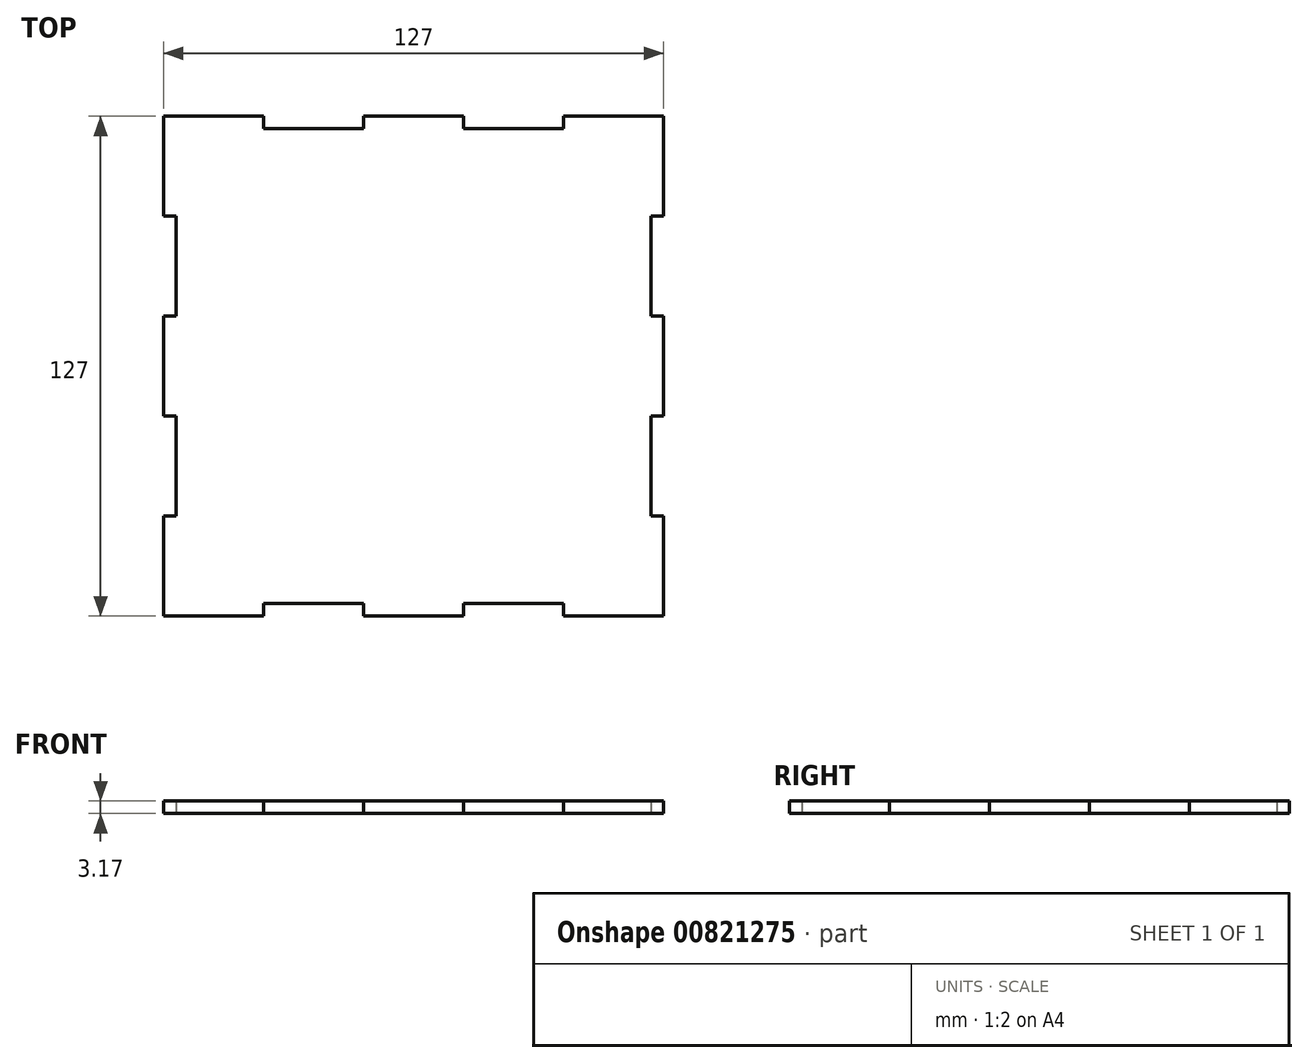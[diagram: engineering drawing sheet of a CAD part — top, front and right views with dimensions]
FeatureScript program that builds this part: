
annotation { "Feature Type Name" : "Feature", "Feature Type Description" : "" }
export const myFeature = defineFeature(function(context is Context, id is Id, definition is map)
    precondition{}
    {
        {
            var Q0;
            Q0=qCreatedBy(makeId("Top.planeOp"),FACE);
            var sketch = newSketch(context, id + "F0", { "sketchPlane" : qUnion([Q0])});
            skLineSegment(sketch, "E0.bottom", {"start": v(-63.5, 63.5) * mm, "end": v(63.5, 63.5) * mm});
            skLineSegment(sketch, "E0.top", {"start": v(-63.5, -63.5) * mm, "end": v(63.5, -63.5) * mm});
            skLineSegment(sketch, "E0.left", {"start": v(-63.5, 63.5) * mm, "end": v(-63.5, -63.5) * mm});
            skLineSegment(sketch, "E0.right", {"start": v(63.5, 63.5) * mm, "end": v(63.5, -63.5) * mm});
            skPoint(sketch, "E0.middle", {"position": v(0, 0) * mm});
            skLineSegment(sketch, "E1", {"start": v(-38.1, 63.5) * mm, "end": v(-38.1, -63.5) * mm});
            skLineSegment(sketch, "E2", {"start": v(-63.5, -38.1) * mm, "end": v(63.5, -38.1) * mm});
            skLineSegment(sketch, "E3.1.0.0", {"start": v(-12.7, 63.5) * mm, "end": v(-12.7, -63.5) * mm});
            skLineSegment(sketch, "E3.2.0.0", {"start": v(12.7, 63.5) * mm, "end": v(12.7, -63.5) * mm});
            skLineSegment(sketch, "E3.3.0.0", {"start": v(38.1, 63.5) * mm, "end": v(38.1, -63.5) * mm});
            skLineSegment(sketch, "E3.direction1", {"start": v(-38.1, -63.5) * mm, "end": v(-12.7, -63.5) * mm, "construction": true});
            skLineSegment(sketch, "E4.0.1.0", {"start": v(-63.5, -12.7) * mm, "end": v(63.5, -12.7) * mm});
            skLineSegment(sketch, "E4.0.2.0", {"start": v(-63.5, 12.7) * mm, "end": v(63.5, 12.7) * mm});
            skLineSegment(sketch, "E4.0.3.0", {"start": v(-63.5, 38.1) * mm, "end": v(63.5, 38.1) * mm});
            skLineSegment(sketch, "E4.1.0.0", {"start": v(-38.1, -38.1) * mm, "end": v(63.5, -38.1) * mm});
            skLineSegment(sketch, "E4.1.1.0", {"start": v(-38.1, -12.7) * mm, "end": v(63.5, -12.7) * mm});
            skLineSegment(sketch, "E4.1.2.0", {"start": v(-38.1, 12.7) * mm, "end": v(63.5, 12.7) * mm});
            skLineSegment(sketch, "E4.1.3.0", {"start": v(-38.1, 38.1) * mm, "end": v(63.5, 38.1) * mm});
            skLineSegment(sketch, "E4.2.0.0", {"start": v(-12.7, -38.1) * mm, "end": v(63.5, -38.1) * mm});
            skLineSegment(sketch, "E4.2.1.0", {"start": v(-12.7, -12.7) * mm, "end": v(63.5, -12.7) * mm});
            skLineSegment(sketch, "E4.2.2.0", {"start": v(-12.7, 12.7) * mm, "end": v(63.5, 12.7) * mm});
            skLineSegment(sketch, "E4.2.3.0", {"start": v(-12.7, 38.1) * mm, "end": v(63.5, 38.1) * mm});
            skLineSegment(sketch, "E4.direction1", {"start": v(-63.5, -38.1) * mm, "end": v(-38.1, -38.1) * mm, "construction": true});
            skLineSegment(sketch, "E4.direction2", {"start": v(-63.5, -38.1) * mm, "end": v(-63.5, -12.7) * mm, "construction": true});
            skLineSegment(sketch, "E5", {"start": v(-63.5, -60.33) * mm, "end": v(63.5, -60.32) * mm});
            skLineSegment(sketch, "E6", {"start": v(-60.33, 63.5) * mm, "end": v(-60.33, -63.5) * mm});
            skLineSegment(sketch, "E7", {"start": v(-63.5, 60.33) * mm, "end": v(63.5, 60.33) * mm});
            skLineSegment(sketch, "E8", {"start": v(60.32, 63.5) * mm, "end": v(60.32, -63.5) * mm});
            skSolve(sketch);
        }
        {
            var Q0;
            {var subQ0=sQuery(id+"F0.wireOp",EDGE,"E6");var subQ1=sQuery(id+"F0.wireOp",EDGE,"E0.bottom");var subQ2=makeQuery(id+"F0.imprint","INTERSECT",VERTEX,{"derivedFrom":[subQ1,subQ0]});Q0=makeQuery(id+"F0.imprint","IMPRINT",FACE,{"disambiguationData":[TD([[makeQuery(id+"F0.imprint","IMPRINT",EDGE,{"disambiguationData":[TD([[subQ2,1.0]])],"derivedFrom":subQ1}),-1.0]])]});}
            var Q1;
            {var subQ0=sQuery(id+"F0.wireOp",EDGE,"E0.right");var subQ1=sQuery(id+"F0.wireOp",EDGE,"E0.bottom");var subQ2=makeQuery(id+"F0.imprint","INTERSECT",VERTEX,{"derivedFrom":[subQ1,subQ0]});Q1=makeQuery(id+"F0.imprint","IMPRINT",FACE,{"disambiguationData":[TD([[makeQuery(id+"F0.imprint","IMPRINT",EDGE,{"disambiguationData":[TD([[subQ2,1.0]])],"derivedFrom":subQ1}),-1.0]])]});}
            var Q2;
            {var subQ0=sQuery(id+"F0.wireOp",EDGE,"E6");var subQ1=sQuery(id+"F0.wireOp",EDGE,"E0.top");var subQ2=makeQuery(id+"F0.imprint","INTERSECT",VERTEX,{"derivedFrom":[subQ1,subQ0]});Q2=makeQuery(id+"F0.imprint","IMPRINT",FACE,{"disambiguationData":[TD([[makeQuery(id+"F0.imprint","IMPRINT",EDGE,{"disambiguationData":[TD([[subQ2,1.0]])],"derivedFrom":subQ1}),1.0]])]});}
            var Q3;
            {var subQ0=sQuery(id+"F0.wireOp",EDGE,"E0.right");var subQ1=sQuery(id+"F0.wireOp",EDGE,"E0.top");var subQ2=makeQuery(id+"F0.imprint","INTERSECT",VERTEX,{"derivedFrom":[subQ1,subQ0]});Q3=makeQuery(id+"F0.imprint","IMPRINT",FACE,{"disambiguationData":[TD([[makeQuery(id+"F0.imprint","IMPRINT",EDGE,{"disambiguationData":[TD([[subQ2,1.0]])],"derivedFrom":subQ1}),1.0]])]});}
            var Q4;
            {var subQ0=sQuery(id+"F0.wireOp",EDGE,"E1");var subQ1=sQuery(id+"F0.wireOp",EDGE,"E0.bottom");var subQ2=makeQuery(id+"F0.imprint","INTERSECT",VERTEX,{"derivedFrom":[subQ1,subQ0]});Q4=makeQuery(id+"F0.imprint","IMPRINT",FACE,{"disambiguationData":[TD([[makeQuery(id+"F0.imprint","IMPRINT",EDGE,{"disambiguationData":[TD([[subQ2,1.0]])],"derivedFrom":subQ1}),-1.0]])]});}
            var Q5;
            {var subQ0=sQuery(id+"F0.wireOp",EDGE,"E3.1.0.0");var subQ1=sQuery(id+"F0.wireOp",EDGE,"E0.bottom");var subQ2=makeQuery(id+"F0.imprint","INTERSECT",VERTEX,{"derivedFrom":[subQ1,subQ0]});Q5=makeQuery(id+"F0.imprint","IMPRINT",FACE,{"disambiguationData":[TD([[makeQuery(id+"F0.imprint","IMPRINT",EDGE,{"disambiguationData":[TD([[subQ2,-1.0]])],"derivedFrom":subQ1}),-1.0]])]});}
            var Q6;
            {var subQ0=sQuery(id+"F0.wireOp",EDGE,"E3.3.0.0");var subQ1=sQuery(id+"F0.wireOp",EDGE,"E0.bottom");var subQ2=makeQuery(id+"F0.imprint","INTERSECT",VERTEX,{"derivedFrom":[subQ1,subQ0]});Q6=makeQuery(id+"F0.imprint","IMPRINT",FACE,{"disambiguationData":[TD([[makeQuery(id+"F0.imprint","IMPRINT",EDGE,{"disambiguationData":[TD([[subQ2,-1.0]])],"derivedFrom":subQ1}),-1.0]])]});}
            var Q7;
            {var subQ0=sQuery(id+"F0.wireOp",EDGE,"E1");var subQ1=sQuery(id+"F0.wireOp",EDGE,"E0.top");var subQ2=makeQuery(id+"F0.imprint","INTERSECT",VERTEX,{"derivedFrom":[subQ1,subQ0]});Q7=makeQuery(id+"F0.imprint","IMPRINT",FACE,{"disambiguationData":[TD([[makeQuery(id+"F0.imprint","IMPRINT",EDGE,{"disambiguationData":[TD([[subQ2,1.0]])],"derivedFrom":subQ1}),1.0]])]});}
            var Q8;
            {var subQ0=sQuery(id+"F0.wireOp",EDGE,"E3.1.0.0");var subQ1=sQuery(id+"F0.wireOp",EDGE,"E0.top");var subQ2=makeQuery(id+"F0.imprint","INTERSECT",VERTEX,{"derivedFrom":[subQ1,subQ0]});Q8=makeQuery(id+"F0.imprint","IMPRINT",FACE,{"disambiguationData":[TD([[makeQuery(id+"F0.imprint","IMPRINT",EDGE,{"disambiguationData":[TD([[subQ2,-1.0]])],"derivedFrom":subQ1}),1.0]])]});}
            var Q9;
            {var subQ0=sQuery(id+"F0.wireOp",EDGE,"E3.3.0.0");var subQ1=sQuery(id+"F0.wireOp",EDGE,"E0.top");var subQ2=makeQuery(id+"F0.imprint","INTERSECT",VERTEX,{"derivedFrom":[subQ1,subQ0]});Q9=makeQuery(id+"F0.imprint","IMPRINT",FACE,{"disambiguationData":[TD([[makeQuery(id+"F0.imprint","IMPRINT",EDGE,{"disambiguationData":[TD([[subQ2,-1.0]])],"derivedFrom":subQ1}),1.0]])]});}
            var Q10;
            {var subQ0=sQuery(id+"F0.wireOp",EDGE,"E7");var subQ1=sQuery(id+"F0.wireOp",EDGE,"E0.left");var subQ2=makeQuery(id+"F0.imprint","INTERSECT",VERTEX,{"derivedFrom":[subQ1,subQ0]});Q10=makeQuery(id+"F0.imprint","IMPRINT",FACE,{"disambiguationData":[TD([[makeQuery(id+"F0.imprint","IMPRINT",EDGE,{"disambiguationData":[TD([[subQ2,-1.0]])],"derivedFrom":subQ1}),1.0]])]});}
            var Q11;
            {var subQ0=sQuery(id+"F0.wireOp",EDGE,"E4.0.2.0");var subQ1=sQuery(id+"F0.wireOp",EDGE,"E0.left");var subQ2=makeQuery(id+"F0.imprint","INTERSECT",VERTEX,{"derivedFrom":[subQ1,subQ0]});Q11=makeQuery(id+"F0.imprint","IMPRINT",FACE,{"disambiguationData":[TD([[makeQuery(id+"F0.imprint","IMPRINT",EDGE,{"disambiguationData":[TD([[subQ2,-1.0]])],"derivedFrom":subQ1}),1.0]])]});}
            var Q12;
            {var subQ0=sQuery(id+"F0.wireOp",EDGE,"E2");var subQ1=sQuery(id+"F0.wireOp",EDGE,"E0.left");var subQ2=makeQuery(id+"F0.imprint","INTERSECT",VERTEX,{"derivedFrom":[subQ1,subQ0]});Q12=makeQuery(id+"F0.imprint","IMPRINT",FACE,{"disambiguationData":[TD([[makeQuery(id+"F0.imprint","IMPRINT",EDGE,{"disambiguationData":[TD([[subQ2,-1.0]])],"derivedFrom":subQ1}),1.0]])]});}
            var Q13;
            {var subQ0=sQuery(id+"F0.wireOp",EDGE,"E7");var subQ1=sQuery(id+"F0.wireOp",EDGE,"E0.right");var subQ2=makeQuery(id+"F0.imprint","INTERSECT",VERTEX,{"derivedFrom":[subQ1,subQ0]});Q13=makeQuery(id+"F0.imprint","IMPRINT",FACE,{"disambiguationData":[TD([[makeQuery(id+"F0.imprint","IMPRINT",EDGE,{"disambiguationData":[TD([[subQ2,-1.0]])],"derivedFrom":subQ1}),-1.0]])]});}
            var Q14;
            {var subQ0=sQuery(id+"F0.wireOp",EDGE,"E4.0.2.0");var subQ1=sQuery(id+"F0.wireOp",EDGE,"E0.right");var subQ2=makeQuery(id+"F0.imprint","INTERSECT",VERTEX,{"derivedFrom":[subQ1,subQ0]});Q14=makeQuery(id+"F0.imprint","IMPRINT",FACE,{"disambiguationData":[TD([[makeQuery(id+"F0.imprint","IMPRINT",EDGE,{"disambiguationData":[TD([[subQ2,-1.0]])],"derivedFrom":subQ1}),-1.0]])]});}
            var Q15;
            {var subQ0=sQuery(id+"F0.wireOp",EDGE,"E5");var subQ1=sQuery(id+"F0.wireOp",EDGE,"E0.right");var subQ2=makeQuery(id+"F0.imprint","INTERSECT",VERTEX,{"derivedFrom":[subQ1,subQ0]});Q15=makeQuery(id+"F0.imprint","IMPRINT",FACE,{"disambiguationData":[TD([[makeQuery(id+"F0.imprint","IMPRINT",EDGE,{"disambiguationData":[TD([[subQ2,1.0]])],"derivedFrom":subQ1}),-1.0]])]});}
            var Q16;
            {var subQ0=sQuery(id+"F0.wireOp",EDGE,"E7");var subQ1=sQuery(id+"F0.wireOp",EDGE,"E1");var subQ2=makeQuery(id+"F0.imprint","INTERSECT",VERTEX,{"derivedFrom":[subQ1,subQ0]});Q16=makeQuery(id+"F0.imprint","IMPRINT",FACE,{"disambiguationData":[TD([[makeQuery(id+"F0.imprint","IMPRINT",EDGE,{"disambiguationData":[TD([[subQ2,-1.0]])],"derivedFrom":subQ1}),-1.0]])]});}
            var Q17;
            {var subQ0=sQuery(id+"F0.wireOp",EDGE,"E7");var subQ1=sQuery(id+"F0.wireOp",EDGE,"E1");var subQ2=makeQuery(id+"F0.imprint","INTERSECT",VERTEX,{"derivedFrom":[subQ1,subQ0]});Q17=makeQuery(id+"F0.imprint","IMPRINT",FACE,{"disambiguationData":[TD([[makeQuery(id+"F0.imprint","IMPRINT",EDGE,{"disambiguationData":[TD([[subQ2,-1.0]])],"derivedFrom":subQ1}),1.0]])]});}
            var Q18;
            {var subQ0=sQuery(id+"F0.wireOp",EDGE,"E7");var subQ1=sQuery(id+"F0.wireOp",EDGE,"E3.2.0.0");var subQ2=makeQuery(id+"F0.imprint","INTERSECT",VERTEX,{"derivedFrom":[subQ1,subQ0]});Q18=makeQuery(id+"F0.imprint","IMPRINT",FACE,{"disambiguationData":[TD([[makeQuery(id+"F0.imprint","IMPRINT",EDGE,{"disambiguationData":[TD([[subQ2,-1.0]])],"derivedFrom":subQ1}),1.0]])]});}
            var Q19;
            {var subQ0=sQuery(id+"F0.wireOp",EDGE,"E7");var subQ1=sQuery(id+"F0.wireOp",EDGE,"E3.3.0.0");var subQ2=makeQuery(id+"F0.imprint","INTERSECT",VERTEX,{"derivedFrom":[subQ1,subQ0]});Q19=makeQuery(id+"F0.imprint","IMPRINT",FACE,{"disambiguationData":[TD([[makeQuery(id+"F0.imprint","IMPRINT",EDGE,{"disambiguationData":[TD([[subQ2,-1.0]])],"derivedFrom":subQ1}),1.0]])]});}
            var Q20;
            {var subQ0=sQuery(id+"F0.wireOp",EDGE,"E4.0.2.0");var subQ1=sQuery(id+"F0.wireOp",EDGE,"E3.3.0.0");var subQ2=makeQuery(id+"F0.imprint","INTERSECT",VERTEX,{"derivedFrom":[subQ1,subQ0]});Q20=makeQuery(id+"F0.imprint","IMPRINT",FACE,{"disambiguationData":[TD([[makeQuery(id+"F0.imprint","IMPRINT",EDGE,{"disambiguationData":[TD([[subQ2,1.0]])],"derivedFrom":subQ1}),1.0]])]});}
            var Q21;
            {var subQ0=sQuery(id+"F0.wireOp",EDGE,"E4.0.2.0");var subQ1=sQuery(id+"F0.wireOp",EDGE,"E3.2.0.0");var subQ2=makeQuery(id+"F0.imprint","INTERSECT",VERTEX,{"derivedFrom":[subQ1,subQ0]});Q21=makeQuery(id+"F0.imprint","IMPRINT",FACE,{"disambiguationData":[TD([[makeQuery(id+"F0.imprint","IMPRINT",EDGE,{"disambiguationData":[TD([[subQ2,1.0]])],"derivedFrom":subQ1}),1.0]])]});}
            var Q22;
            {var subQ0=sQuery(id+"F0.wireOp",EDGE,"E4.0.2.0");var subQ1=sQuery(id+"F0.wireOp",EDGE,"E3.1.0.0");var subQ2=makeQuery(id+"F0.imprint","INTERSECT",VERTEX,{"derivedFrom":[subQ1,subQ0]});Q22=makeQuery(id+"F0.imprint","IMPRINT",FACE,{"disambiguationData":[TD([[makeQuery(id+"F0.imprint","IMPRINT",EDGE,{"disambiguationData":[TD([[subQ2,1.0]])],"derivedFrom":subQ1}),1.0]])]});}
            var Q23;
            {var subQ0=sQuery(id+"F0.wireOp",EDGE,"E4.0.2.0");var subQ1=sQuery(id+"F0.wireOp",EDGE,"E1");var subQ2=makeQuery(id+"F0.imprint","INTERSECT",VERTEX,{"derivedFrom":[subQ1,subQ0]});Q23=makeQuery(id+"F0.imprint","IMPRINT",FACE,{"disambiguationData":[TD([[makeQuery(id+"F0.imprint","IMPRINT",EDGE,{"disambiguationData":[TD([[subQ2,1.0]])],"derivedFrom":subQ1}),1.0]])]});}
            var Q24;
            {var subQ0=sQuery(id+"F0.wireOp",EDGE,"E4.0.2.0");var subQ1=sQuery(id+"F0.wireOp",EDGE,"E1");var subQ2=makeQuery(id+"F0.imprint","INTERSECT",VERTEX,{"derivedFrom":[subQ1,subQ0]});Q24=makeQuery(id+"F0.imprint","IMPRINT",FACE,{"disambiguationData":[TD([[makeQuery(id+"F0.imprint","IMPRINT",EDGE,{"disambiguationData":[TD([[subQ2,1.0]])],"derivedFrom":subQ1}),-1.0]])]});}
            var Q25;
            {var subQ0=sQuery(id+"F0.wireOp",EDGE,"E4.0.2.0");var subQ1=sQuery(id+"F0.wireOp",EDGE,"E1");var subQ2=makeQuery(id+"F0.imprint","INTERSECT",VERTEX,{"derivedFrom":[subQ1,subQ0]});Q25=makeQuery(id+"F0.imprint","IMPRINT",FACE,{"disambiguationData":[TD([[makeQuery(id+"F0.imprint","IMPRINT",EDGE,{"disambiguationData":[TD([[subQ2,-1.0]])],"derivedFrom":subQ1}),-1.0]])]});}
            var Q26;
            {var subQ0=sQuery(id+"F0.wireOp",EDGE,"E4.0.2.0");var subQ1=sQuery(id+"F0.wireOp",EDGE,"E1");var subQ2=makeQuery(id+"F0.imprint","INTERSECT",VERTEX,{"derivedFrom":[subQ1,subQ0]});Q26=makeQuery(id+"F0.imprint","IMPRINT",FACE,{"disambiguationData":[TD([[makeQuery(id+"F0.imprint","IMPRINT",EDGE,{"disambiguationData":[TD([[subQ2,-1.0]])],"derivedFrom":subQ1}),1.0]])]});}
            var Q27;
            {var subQ0=sQuery(id+"F0.wireOp",EDGE,"E4.0.1.0");var subQ1=sQuery(id+"F0.wireOp",EDGE,"E3.1.0.0");var subQ2=makeQuery(id+"F0.imprint","INTERSECT",VERTEX,{"derivedFrom":[subQ1,subQ0]});Q27=makeQuery(id+"F0.imprint","IMPRINT",FACE,{"disambiguationData":[TD([[makeQuery(id+"F0.imprint","IMPRINT",EDGE,{"disambiguationData":[TD([[subQ2,1.0]])],"derivedFrom":subQ1}),1.0]])]});}
            var Q28;
            {var subQ0=sQuery(id+"F0.wireOp",EDGE,"E4.0.1.0");var subQ1=sQuery(id+"F0.wireOp",EDGE,"E3.2.0.0");var subQ2=makeQuery(id+"F0.imprint","INTERSECT",VERTEX,{"derivedFrom":[subQ1,subQ0]});Q28=makeQuery(id+"F0.imprint","IMPRINT",FACE,{"disambiguationData":[TD([[makeQuery(id+"F0.imprint","IMPRINT",EDGE,{"disambiguationData":[TD([[subQ2,1.0]])],"derivedFrom":subQ1}),1.0]])]});}
            var Q29;
            {var subQ0=sQuery(id+"F0.wireOp",EDGE,"E4.0.1.0");var subQ1=sQuery(id+"F0.wireOp",EDGE,"E3.3.0.0");var subQ2=makeQuery(id+"F0.imprint","INTERSECT",VERTEX,{"derivedFrom":[subQ1,subQ0]});Q29=makeQuery(id+"F0.imprint","IMPRINT",FACE,{"disambiguationData":[TD([[makeQuery(id+"F0.imprint","IMPRINT",EDGE,{"disambiguationData":[TD([[subQ2,1.0]])],"derivedFrom":subQ1}),1.0]])]});}
            var Q30;
            {var subQ0=sQuery(id+"F0.wireOp",EDGE,"E3.3.0.0");var subQ1=sQuery(id+"F0.wireOp",EDGE,"E2");var subQ2=makeQuery(id+"F0.imprint","INTERSECT",VERTEX,{"derivedFrom":[subQ1,subQ0]});Q30=makeQuery(id+"F0.imprint","IMPRINT",FACE,{"disambiguationData":[TD([[makeQuery(id+"F0.imprint","IMPRINT",EDGE,{"disambiguationData":[TD([[subQ2,-1.0]])],"derivedFrom":subQ1}),1.0]])]});}
            var Q31;
            {var subQ0=sQuery(id+"F0.wireOp",EDGE,"E3.2.0.0");var subQ1=sQuery(id+"F0.wireOp",EDGE,"E2");var subQ2=makeQuery(id+"F0.imprint","INTERSECT",VERTEX,{"derivedFrom":[subQ1,subQ0]});Q31=makeQuery(id+"F0.imprint","IMPRINT",FACE,{"disambiguationData":[TD([[makeQuery(id+"F0.imprint","IMPRINT",EDGE,{"disambiguationData":[TD([[subQ2,-1.0]])],"derivedFrom":subQ1}),1.0]])]});}
            var Q32;
            {var subQ0=sQuery(id+"F0.wireOp",EDGE,"E3.1.0.0");var subQ1=sQuery(id+"F0.wireOp",EDGE,"E2");var subQ2=makeQuery(id+"F0.imprint","INTERSECT",VERTEX,{"derivedFrom":[subQ1,subQ0]});Q32=makeQuery(id+"F0.imprint","IMPRINT",FACE,{"disambiguationData":[TD([[makeQuery(id+"F0.imprint","IMPRINT",EDGE,{"disambiguationData":[TD([[subQ2,-1.0]])],"derivedFrom":subQ1}),1.0]])]});}
            var Q33;
            {var subQ0=sQuery(id+"F0.wireOp",EDGE,"E4.0.1.0");var subQ1=sQuery(id+"F0.wireOp",EDGE,"E1");var subQ2=makeQuery(id+"F0.imprint","INTERSECT",VERTEX,{"derivedFrom":[subQ1,subQ0]});Q33=makeQuery(id+"F0.imprint","IMPRINT",FACE,{"disambiguationData":[TD([[makeQuery(id+"F0.imprint","IMPRINT",EDGE,{"disambiguationData":[TD([[subQ2,-1.0]])],"derivedFrom":subQ1}),1.0]])]});}
            var Q34;
            {var subQ0=sQuery(id+"F0.wireOp",EDGE,"E4.0.1.0");var subQ1=sQuery(id+"F0.wireOp",EDGE,"E1");var subQ2=makeQuery(id+"F0.imprint","INTERSECT",VERTEX,{"derivedFrom":[subQ1,subQ0]});Q34=makeQuery(id+"F0.imprint","IMPRINT",FACE,{"disambiguationData":[TD([[makeQuery(id+"F0.imprint","IMPRINT",EDGE,{"disambiguationData":[TD([[subQ2,-1.0]])],"derivedFrom":subQ1}),-1.0]])]});}
            var Q35;
            {var subQ0=sQuery(id+"F0.wireOp",EDGE,"E5");var subQ1=sQuery(id+"F0.wireOp",EDGE,"E1");var subQ2=makeQuery(id+"F0.imprint","INTERSECT",VERTEX,{"derivedFrom":[subQ1,subQ0]});Q35=makeQuery(id+"F0.imprint","IMPRINT",FACE,{"disambiguationData":[TD([[makeQuery(id+"F0.imprint","IMPRINT",EDGE,{"disambiguationData":[TD([[subQ2,1.0]])],"derivedFrom":subQ1}),-1.0]])]});}
            var Q36;
            {var subQ0=sQuery(id+"F0.wireOp",EDGE,"E5");var subQ1=sQuery(id+"F0.wireOp",EDGE,"E1");var subQ2=makeQuery(id+"F0.imprint","INTERSECT",VERTEX,{"derivedFrom":[subQ1,subQ0]});Q36=makeQuery(id+"F0.imprint","IMPRINT",FACE,{"disambiguationData":[TD([[makeQuery(id+"F0.imprint","IMPRINT",EDGE,{"disambiguationData":[TD([[subQ2,1.0]])],"derivedFrom":subQ1}),1.0]])]});}
            var Q37;
            {var subQ0=sQuery(id+"F0.wireOp",EDGE,"E3.2.0.0");var subQ1=sQuery(id+"F0.wireOp",EDGE,"E2");var subQ2=makeQuery(id+"F0.imprint","INTERSECT",VERTEX,{"derivedFrom":[subQ1,subQ0]});Q37=makeQuery(id+"F0.imprint","IMPRINT",FACE,{"disambiguationData":[TD([[makeQuery(id+"F0.imprint","IMPRINT",EDGE,{"disambiguationData":[TD([[subQ2,-1.0]])],"derivedFrom":subQ1}),-1.0]])]});}
            var Q38;
            {var subQ0=sQuery(id+"F0.wireOp",EDGE,"E3.3.0.0");var subQ1=sQuery(id+"F0.wireOp",EDGE,"E2");var subQ2=makeQuery(id+"F0.imprint","INTERSECT",VERTEX,{"derivedFrom":[subQ1,subQ0]});Q38=makeQuery(id+"F0.imprint","IMPRINT",FACE,{"disambiguationData":[TD([[makeQuery(id+"F0.imprint","IMPRINT",EDGE,{"disambiguationData":[TD([[subQ2,-1.0]])],"derivedFrom":subQ1}),-1.0]])]});}
            var Q39;
            {var subQ0=sQuery(id+"F0.wireOp",EDGE,"E7");var subQ1=sQuery(id+"F0.wireOp",EDGE,"E3.1.0.0");var subQ2=makeQuery(id+"F0.imprint","INTERSECT",VERTEX,{"derivedFrom":[subQ1,subQ0]});Q39=makeQuery(id+"F0.imprint","IMPRINT",FACE,{"disambiguationData":[TD([[makeQuery(id+"F0.imprint","IMPRINT",EDGE,{"disambiguationData":[TD([[subQ2,-1.0]])],"derivedFrom":subQ1}),1.0]])]});}
            var Q40;
            {var subQ0=sQuery(id+"F0.wireOp",EDGE,"E3.1.0.0");var subQ1=sQuery(id+"F0.wireOp",EDGE,"E2");var subQ2=makeQuery(id+"F0.imprint","INTERSECT",VERTEX,{"derivedFrom":[subQ1,subQ0]});Q40=makeQuery(id+"F0.imprint","IMPRINT",FACE,{"disambiguationData":[TD([[makeQuery(id+"F0.imprint","IMPRINT",EDGE,{"disambiguationData":[TD([[subQ2,-1.0]])],"derivedFrom":subQ1}),-1.0]])]});}
            extrude(context, id + "F1", {"entities" : qUnion([Q0, Q1, Q2, Q3, Q4, Q5, Q6, Q7, Q8, Q9, Q10, Q11, Q12, Q13, Q14, Q15, Q16, Q17, Q18, Q19, Q20, Q21, Q22, Q23, Q24, Q25, Q26, Q27, Q28, Q29, Q30, Q31, Q32, Q33, Q34, Q35, Q36, Q37, Q38, Q39, Q40]), "depth" : 3.17 * mm, "offsetDistance" : 25.4 * mm});
        }
    });
